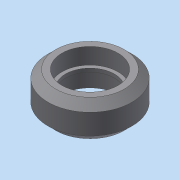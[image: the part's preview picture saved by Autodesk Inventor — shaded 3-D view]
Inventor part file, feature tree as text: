
AUTODESK INVENTOR PART (.ipt)
format: ipt  version: 2013 SP2 (Build 170200200, 200)  size: 102,912 bytes
history: native  units: mm
features: revolve x1, mirror x1, sketch x1
ambient origin geometry x8: Origin, YZ Plane, XZ Plane, XY Plane, X Axis, Y Axis, Z Axis, Center Point
bodies: Solid1 (feature_tree)
feature tree (3):
  revolve  "Revolution1"  [1 undecoded]
  mirror  "Mirror1"
  sketch  "Sketch1"  dims[d2=23.89mm d4=2.945mm d5=19.54mm d6=5.115mm d7=15.974mm d8=0.5mm d9=13.89mm d10=90.0deg]
note: 1 required parameter value undecoded (feature->parameter linkage not recoverable at this tier; creation-order binding heuristic only, values carry confidence <= 0.55)
